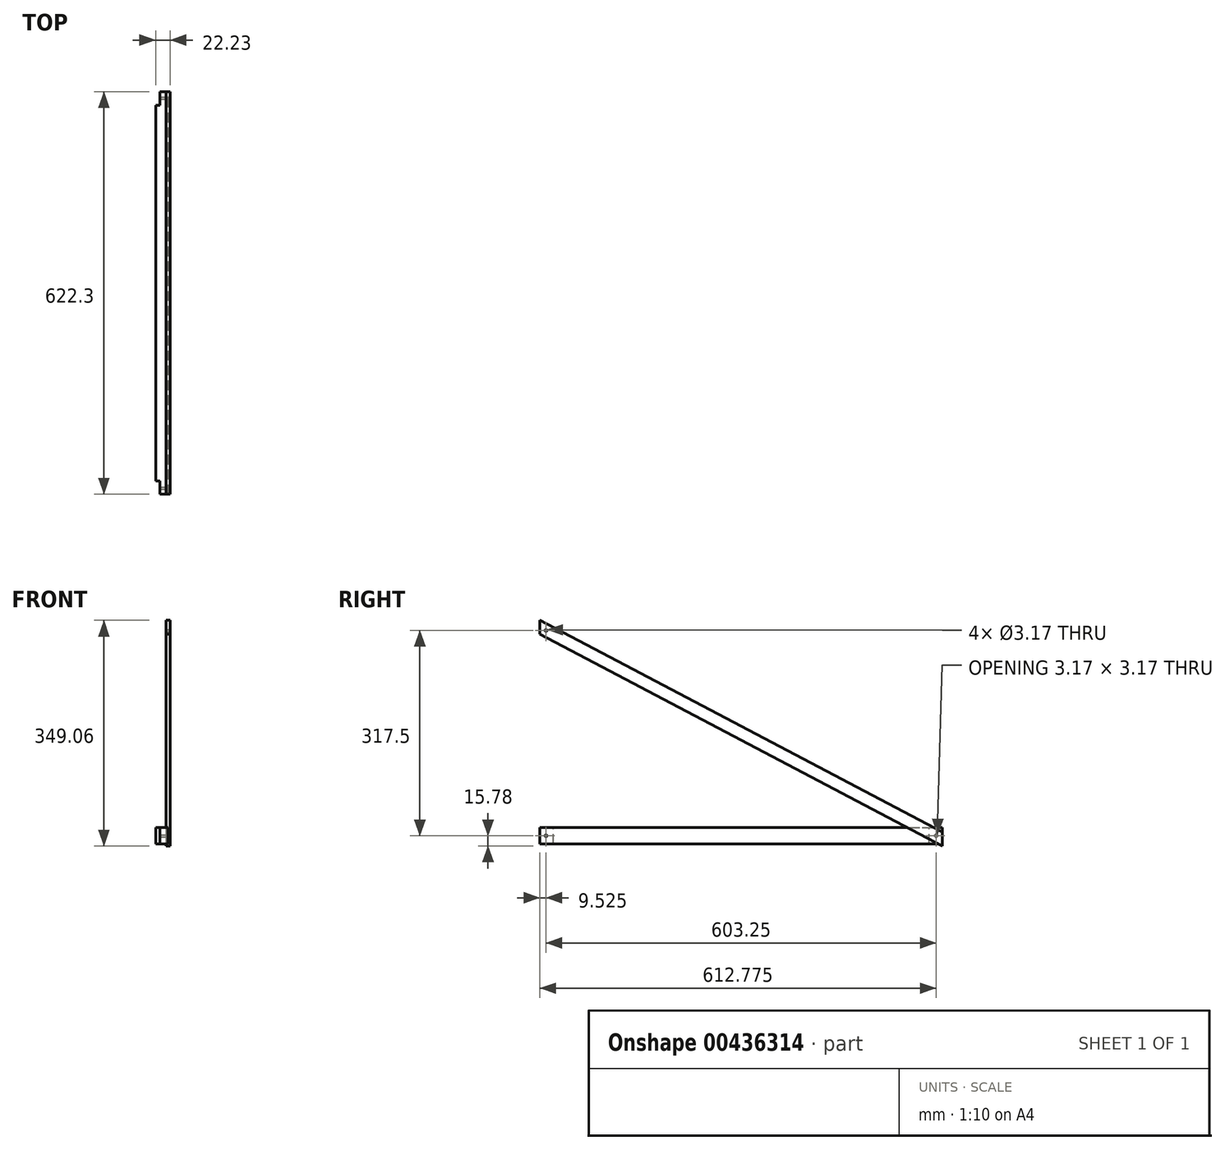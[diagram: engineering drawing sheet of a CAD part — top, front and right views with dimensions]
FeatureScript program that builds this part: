
annotation { "Feature Type Name" : "Feature", "Feature Type Description" : "" }
export const myFeature = defineFeature(function(context is Context, id is Id, definition is map)
    precondition{}
    {
        {
            var Q0;
            Q0=qCreatedBy(makeId("Front.planeOp"),FACE);
            var sketch = newSketch(context, id + "F0", { "sketchPlane" : qUnion([Q0])});
            skLineSegment(sketch, "E0.bottom", {"start": v(9.53, -12.7) * mm, "end": v(-9.53, -12.7) * mm});
            skLineSegment(sketch, "E0.top", {"start": v(9.53, 12.7) * mm, "end": v(-9.52, 12.7) * mm});
            skLineSegment(sketch, "E0.left", {"start": v(9.53, -12.7) * mm, "end": v(9.53, 12.7) * mm});
            skLineSegment(sketch, "E0.right", {"start": v(-9.53, -12.7) * mm, "end": v(-9.52, 12.7) * mm});
            skPoint(sketch, "E0.middle", {"position": v(0, 0) * mm});
            skSolve(sketch);
        }
        {
            var Q0;
            Q0 = qSketchRegion(id + "F0", true);
            extrude(context, id + "F1", {"entities" : qUnion([Q0]), "endBound" : BoundingType.SYMMETRIC, "depth" : 622.3 * mm});
        }
        {
            var Q0;
            Q0=makeQuery(id+"F1.opExtrude","SWEPT_FACE",FACE,{"disambiguationData":[OSD([sQuery(id+"F0.wireOp",EDGE,"E0.left")])]});
            var sketch = newSketch(context, id + "F2", { "sketchPlane" : qUnion([Q0])});
            skPoint(sketch, "E1", {"position": v(-301.63, 0) * mm});
            skPoint(sketch, "E2", {"position": v(301.63, 0) * mm});
            skSolve(sketch);
        }
        {
            var Q0;
            Q0=sQuery(id+"F2.wireOp",VERTEX,"E1");
            var Q1;
            Q1=sQuery(id+"F2.wireOp",VERTEX,"E2");
            var Q2;
            Q2=makeQuery(id+"F1.opExtrude","SWEPT_BODY",BODY,{"disambiguationData":[OSD([sQuery(id+"F0.wireOp",EDGE,"E0.bottom"),sQuery(id+"F0.wireOp",EDGE,"E0.top"),sQuery(id+"F0.wireOp",EDGE,"E0.left"),sQuery(id+"F0.wireOp",EDGE,"E0.right")])]});
            hole(context, id + "F3", {"style" : HoleStyle.SIMPLE, "endStyle" : HoleEndStyle.THROUGH, "holeDiameter" : 3.17 * mm, "isTappedThrough" : true, "tappedDepth" : 12.7 * mm, "tapClearance" : 3, "locations" : qUnion([Q0, Q1]), "scope" : qUnion([Q2])});
        }
        {
            var Q0;
            Q0=makeQuery(id+"F1.opExtrude","SWEPT_FACE",FACE,{"disambiguationData":[OSD([sQuery(id+"F0.wireOp",EDGE,"E0.top")])]});
            var sketch = newSketch(context, id + "F4", { "sketchPlane" : qUnion([Q0])});
            skLineSegment(sketch, "E3.bottom", {"start": v(-9.52, -311.15) * mm, "end": v(-3.18, -311.15) * mm});
            skLineSegment(sketch, "E3.top", {"start": v(-9.53, -290.51) * mm, "end": v(-3.18, -290.51) * mm});
            skLineSegment(sketch, "E3.left", {"start": v(-9.52, -311.15) * mm, "end": v(-9.53, -290.51) * mm});
            skLineSegment(sketch, "E3.right", {"start": v(-3.18, -311.15) * mm, "end": v(-3.18, -290.51) * mm});
            skLineSegment(sketch, "E4.bottom", {"start": v(-9.52, 311.15) * mm, "end": v(-3.18, 311.15) * mm});
            skLineSegment(sketch, "E4.top", {"start": v(-9.53, 290.51) * mm, "end": v(-3.18, 290.51) * mm});
            skLineSegment(sketch, "E4.left", {"start": v(-9.53, 311.15) * mm, "end": v(-9.53, 290.51) * mm});
            skLineSegment(sketch, "E4.right", {"start": v(-3.18, 311.15) * mm, "end": v(-3.18, 290.51) * mm});
            skSolve(sketch);
        }
        {
            var Q0;
            Q0 = qSketchRegion(id + "F4", true);
            extrude(context, id + "F5", {"entities" : qUnion([Q0]), "operationType" : NewBodyOperationType.REMOVE, "endBound" : BoundingType.THROUGH_ALL, "oppositeDirection" : true, "depth" : 25.4 * mm});
        }
        {
            var Q0;
            Q0=makeQuery(id+"F1.opExtrude","SWEPT_FACE",FACE,{"disambiguationData":[OSD([sQuery(id+"F0.wireOp",EDGE,"E0.left")])]});
            var sketch = newSketch(context, id + "F6", { "sketchPlane" : qUnion([Q0])});
            skLineSegment(sketch, "E5.bottom", {"start": v(301.63, 0) * mm, "end": v(-301.63, 0) * mm, "construction": true});
            skLineSegment(sketch, "E5.top", {"start": v(301.62, 317.5) * mm, "end": v(-301.63, 317.5) * mm, "construction": true});
            skLineSegment(sketch, "E5.left", {"start": v(301.63, 0) * mm, "end": v(301.62, 317.5) * mm, "construction": true});
            skLineSegment(sketch, "E5.right", {"start": v(-301.63, 0) * mm, "end": v(-301.63, 317.5) * mm, "construction": true});
            skLineSegment(sketch, "E6", {"start": v(-301.63, 317.5) * mm, "end": v(301.63, 0) * mm, "construction": true});
            skSolve(sketch);
        }
        {
            var Q0;
            Q0=makeQuery(id+"F1.opExtrude","CAP_FACE",FACE,{"disambiguationData":[OSD([sQuery(id+"F0.wireOp",EDGE,"E0.bottom"),sQuery(id+"F0.wireOp",EDGE,"E0.top"),sQuery(id+"F0.wireOp",EDGE,"E0.left"),sQuery(id+"F0.wireOp",EDGE,"E0.right")])],"isStart":false});
            cPlane(context, id + "F7", {"entities" : qUnion([Q0]), "cplaneType" : CPlaneType.OFFSET, "offset" : 0 * mm, "width" : 152.4 * mm, "height" : 152.4 * mm});
        }
        {
            var Q0;
            Q0=makeQuery(id+"F1.opExtrude","CAP_FACE",FACE,{"disambiguationData":[OSD([sQuery(id+"F0.wireOp",EDGE,"E0.bottom"),sQuery(id+"F0.wireOp",EDGE,"E0.top"),sQuery(id+"F0.wireOp",EDGE,"E0.left"),sQuery(id+"F0.wireOp",EDGE,"E0.right")])],"isStart":true});
            cPlane(context, id + "F8", {"entities" : qUnion([Q0]), "cplaneType" : CPlaneType.OFFSET, "offset" : 0 * mm, "width" : 152.4 * mm, "height" : 152.4 * mm});
        }
        {
            var Q0;
            Q0=sQuery(id+"F6.wireOp",EDGE,"E6");
            cPoint(context, id + "F9", {"entities" : qUnion([Q0]), "parameter" : 0.5});
        }
        {
            var Q0;
            Q0=sQuery(id+"F6.wireOp",EDGE,"E6");
            var Q1;
            Q1 = qCreatedBy(id + "F9" ,VERTEX);
            cPlane(context, id + "F10", {"entities" : qUnion([Q0, Q1]), "cplaneType" : CPlaneType.LINE_POINT, "offset" : 25.4 * mm, "width" : 152.4 * mm, "height" : 152.4 * mm});
        }
        {
            var Q0;
            Q0=qCreatedBy(id+"F10.planeOp",FACE);
            var sketch = newSketch(context, id + "F11", { "sketchPlane" : qUnion([Q0])});
            skLineSegment(sketch, "E7.bottom", {"start": v(-6.35, 130.96) * mm, "end": v(-12.7, 130.96) * mm});
            skLineSegment(sketch, "E7.top", {"start": v(-6.35, 150) * mm, "end": v(-12.7, 150) * mm});
            skLineSegment(sketch, "E7.left", {"start": v(-6.35, 130.96) * mm, "end": v(-6.35, 150) * mm});
            skLineSegment(sketch, "E7.right", {"start": v(-12.7, 130.96) * mm, "end": v(-12.7, 150) * mm});
            skPoint(sketch, "E7.middle", {"position": v(-9.53, 140.48) * mm});
            skSolve(sketch);
        }
        {
            var Q0;
            Q0 = qSketchRegion(id + "F11", true);
            var Q1;
            Q1=qCreatedBy(id+"F7.planeOp",FACE);
            var Q2;
            Q2=qCreatedBy(id+"F8.planeOp",FACE);
            extrude(context, id + "F12", {"entities" : qUnion([Q0]), "endBound" : BoundingType.UP_TO_SURFACE, "oppositeDirection" : true, "endBoundEntityFace" : qUnion([Q1]), "depth" : 25.4 * mm, "hasSecondDirection" : true, "secondDirectionBound" : SecondDirectionBoundingType.UP_TO_SURFACE, "secondDirectionOppositeDirection" : false, "secondDirectionBoundEntityFace" : qUnion([Q2]), "secondDirectionDepth" : 25.4 * mm});
        }
        {
            var Q0;
            Q0=makeQuery(id+"F12.opExtrude","SWEPT_FACE",FACE,{"disambiguationData":[OSD([sQuery(id+"F11.wireOp",EDGE,"E7.right")])]});
            var sketch = newSketch(context, id + "F13", { "sketchPlane" : qUnion([Q0])});
            skPoint(sketch, "E8", {"position": v(-301.63, 317.5) * mm});
            skPoint(sketch, "E9", {"position": v(301.63, 0) * mm});
            skSolve(sketch);
        }
        {
            var Q0;
            Q0=sQuery(id+"F13.wireOp",VERTEX,"E8");
            var Q1;
            Q1=sQuery(id+"F13.wireOp",VERTEX,"E9");
            var Q2;
            Q2=makeQuery(id+"F12.opExtrude","SWEPT_BODY",BODY,{"disambiguationData":[OSD([sQuery(id+"F11.wireOp",EDGE,"E7.bottom"),sQuery(id+"F11.wireOp",EDGE,"E7.top"),sQuery(id+"F11.wireOp",EDGE,"E7.left"),sQuery(id+"F11.wireOp",EDGE,"E7.right")])]});
            hole(context, id + "F14", {"style" : HoleStyle.SIMPLE, "endStyle" : HoleEndStyle.THROUGH, "holeDiameter" : 3.17 * mm, "isTappedThrough" : true, "tappedDepth" : 12.7 * mm, "tapClearance" : 3, "locations" : qUnion([Q0, Q1]), "scope" : qUnion([Q2])});
        }
    });
